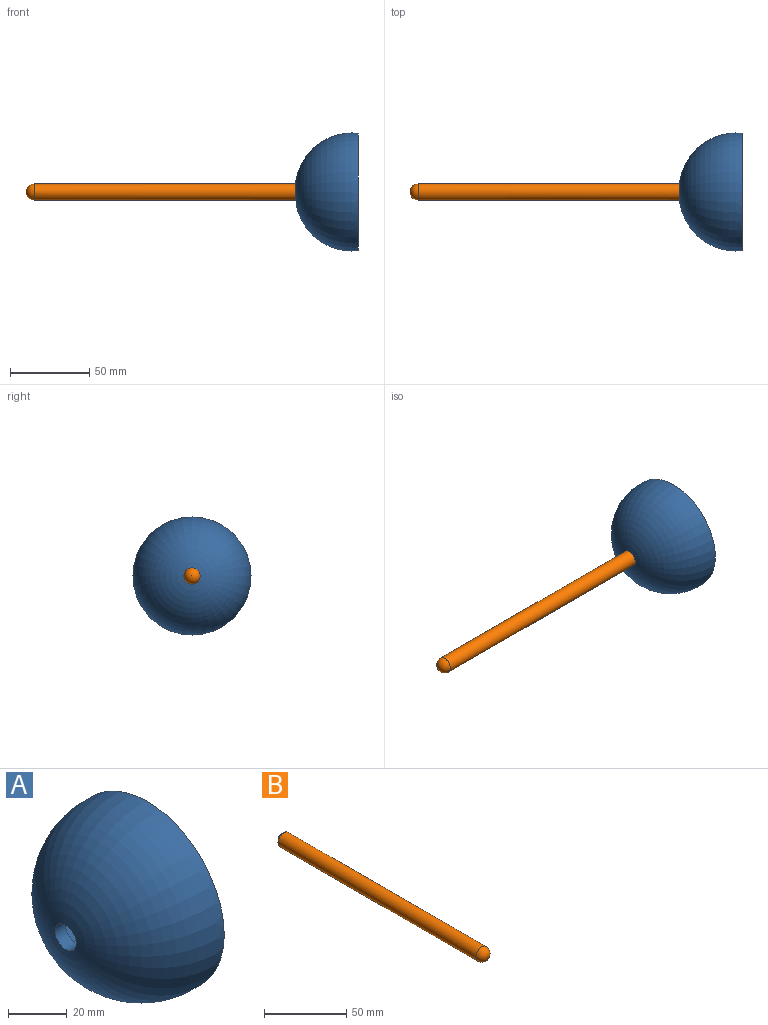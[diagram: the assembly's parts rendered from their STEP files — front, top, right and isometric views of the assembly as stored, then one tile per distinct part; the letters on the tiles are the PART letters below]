
ASSEMBLY  parts=2 mates=1
PART A: 4 faces, bbox 39.5x74.6x74.4 mm
  f0: torus R=2.95mm, axis (-1,0,0), area 7801.8mm2, adj f1,f3
  f1: plane 74.24x74.24mm, normal (1,0,0), area 572.1mm2, adj f0,f2
  f2: torus R=1.17mm, axis (-1,0,0), area 9381.2mm2, adj f1,f3
  f3: cylinder r=5.08mm len=10.16mm, axis (-1,0,0), area 162.1mm2, adj f0,f2
PART B: 4 faces, bbox 10.2x177.8x10.2 mm
  f0: cylinder r=5.08mm len=170.18mm, axis (0,1,0), area 5431.9mm2, adj f2,f3
  f1: plane 5.08x5.08mm, normal (0,1,0), area 20.3mm2, adj f3
  f2: sphere r=5.08mm, area 162.1mm2, adj f0
  f3: cone r=5.08mm half-angle=45deg, axis (0,-1,0), area 86mm2, adj f0,f1
PLACE A t=(-62.69,5.97,-40.25)mm
PLACE B rot(axis=(-0.58,-0.58,-0.58),120deg) t=(-55.07,5.97,-40.25)mm
MATE fastened B.f0 <-> A.f0  axis (-1,0,0) through (-57.61,5.97,-40.25)mm
